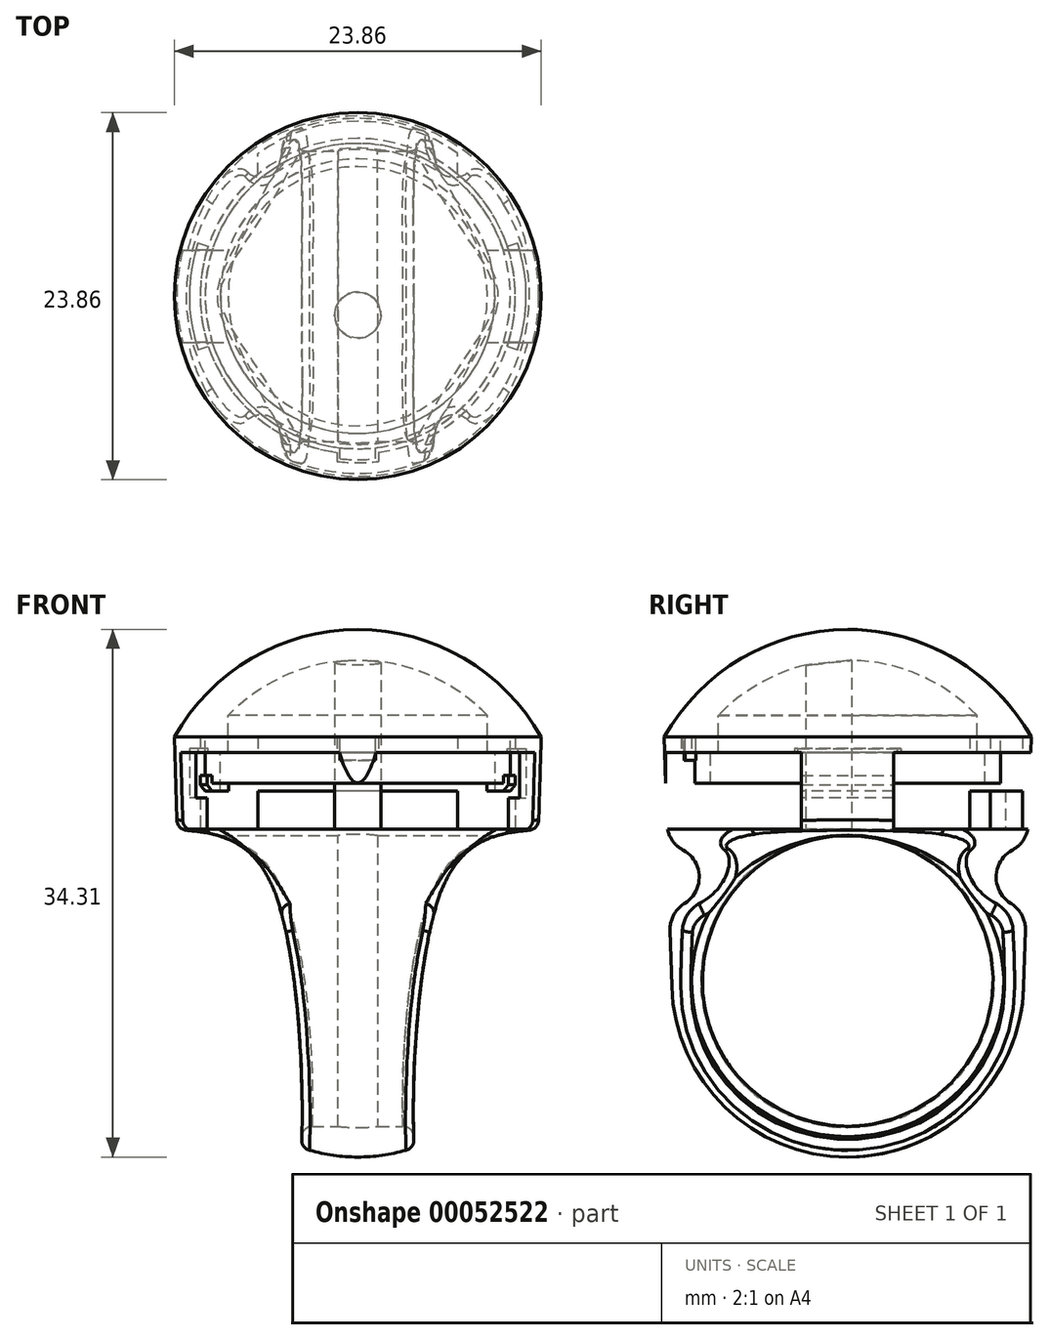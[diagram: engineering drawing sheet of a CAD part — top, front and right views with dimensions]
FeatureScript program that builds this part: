
annotation { "Feature Type Name" : "Feature", "Feature Type Description" : "" }
export const myFeature = defineFeature(function(context is Context, id is Id, definition is map)
    precondition{}
    {
        {
            var Q0;
            Q0=qCreatedBy(makeId("Top.planeOp"),FACE);
            var sketch = newSketch(context, id + "F0", { "sketchPlane" : qUnion([Q0])});
            skArc(sketch, "E0", {"start": v(1.35, -10.16) * mm, "mid": v(9.86, -2.8) * mm, "end": v(6.5, 7.93) * mm});
            skLineSegment(sketch, "E1.rect.left", {"start": v(1.35, -10.75) * mm, "end": v(1.35, -10.16) * mm});
            skLineSegment(sketch, "E1.rect.right", {"start": v(-1.35, -10.75) * mm, "end": v(-1.35, -10.16) * mm});
            skPoint(sketch, "E1.rect.middle", {"position": v(0, -10.25) * mm});
            skPoint(sketch, "E2.orphan", {"position": v(-1.35, -9.75) * mm});
            skPoint(sketch, "E3.orphan", {"position": v(1.35, -9.75) * mm});
            skArc(sketch, "E4", {"start": v(-1.35, -10.75) * mm, "mid": v(0, -10.83) * mm, "end": v(1.35, -10.75) * mm});
            skPoint(sketch, "E4.second.point", {"position": v(1.35, 11.29) * mm});
            skLineSegment(sketch, "E5", {"start": v(-6.5, 9.27) * mm, "end": v(-6.5, 7.93) * mm});
            skLineSegment(sketch, "E6", {"start": v(6.5, 9.27) * mm, "end": v(6.5, 7.93) * mm});
            skArc(sketch, "E7.trimOffspring", {"start": v(-6.5, 7.93) * mm, "mid": v(-9.86, -2.8) * mm, "end": v(-1.35, -10.16) * mm});
            skArc(sketch, "E8.trimOffspring", {"start": v(6.5, 9.27) * mm, "mid": v(0, 11.37) * mm, "end": v(-6.5, 9.27) * mm});
            skSolve(sketch);
        }
        {
            var Q0;
            Q0 = qSketchRegion(id + "F0", true);
            extrude(context, id + "F1", {"entities" : qUnion([Q0]), "depth" : 5 * mm});
        }
        {
            var Q0;
            Q0=qCreatedBy(makeId("Right.planeOp"),FACE);
            var sketch = newSketch(context, id + "F2", { "sketchPlane" : qUnion([Q0])});
            skArc(sketch, "E9", {"start": v(0, -21.3) * mm, "mid": v(7.98, -18.08) * mm, "end": v(11.44, -10.2) * mm});
            skLineSegment(sketch, "E10", {"start": v(11.44, -10.2) * mm, "end": v(11.55, -6.57) * mm});
            skLineSegment(sketch, "E11", {"start": v(0, 13) * mm, "end": v(0, -9.86) * mm});
            skPoint(sketch, "E12.center.orphan", {"position": v(0, -16.43) * mm});
            skArc(sketch, "E13", {"start": v(11.99, 7.98) * mm, "mid": v(6.44, 11.57) * mm, "end": v(0, 13) * mm});
            skLineSegment(sketch, "E14", {"start": v(0, -9.86) * mm, "end": v(0, -21.3) * mm});
            skCircle(sketch, "E15", {"center": v(0, -9.86) * mm, "radius": 9.54 * mm});
            skArc(sketch, "E16", {"start": v(10.7, -1.35) * mm, "mid": v(9.66, -3.05) * mm, "end": v(10.6, -4.8) * mm});
            skLineSegment(sketch, "E17.trimOffspring", {"start": v(11.76, 0.36) * mm, "end": v(11.99, 7.98) * mm});
            skPoint(sketch, "E18.visualSharp", {"position": v(11.72, -1.1) * mm});
            skArc(sketch, "E18.filletArc", {"start": v(10.7, -1.35) * mm, "mid": v(11.46, -0.64) * mm, "end": v(11.76, 0.36) * mm});
            skPoint(sketch, "E19.visualSharp", {"position": v(11.6, -5.1) * mm});
            skArc(sketch, "E19.filletArc", {"start": v(11.55, -6.57) * mm, "mid": v(11.31, -5.56) * mm, "end": v(10.6, -4.8) * mm});
            skSolve(sketch);
        }
        {
            var Q0;
            Q0 = qSketchRegion(id + "F2", true);
            var Q1;
            Q1=sQuery(id+"F2.wireOp",EDGE,"E14");
            revolve(context, id + "F3", {"entities" : qUnion([Q0]), "axis" : qUnion([Q1]), "revolveType" : RevolveType.FULL});
        }
        {
            var Q0;
            Q0=qCreatedBy(makeId("Right.planeOp"),FACE);
            var sketch = newSketch(context, id + "F4", { "sketchPlane" : qUnion([Q0])});
            skCircle(sketch, "E20", {"center": v(0, -9.86) * mm, "radius": 9.45 * mm});
            skSolve(sketch);
        }
        {
            var Q0;
            Q0 = qSketchRegion(id + "F4", true);
            extrude(context, id + "F5", {"entities" : qUnion([Q0]), "operationType" : NewBodyOperationType.REMOVE, "endBound" : BoundingType.SYMMETRIC, "oppositeDirection" : true, "depth" : 25 * mm});
        }
        {
            var Q0;
            Q0=makeQuery(id+"F0.imprint","IMPRINT",FACE,{"disambiguationData":[TD([[makeQuery(id+"F0.imprint","IMPRINT",EDGE,{"derivedFrom":sQuery(id+"F0.wireOp",EDGE,"E0")}),1.0]])]});
            extrude(context, id + "F6", {"entities" : qUnion([Q0]), "operationType" : NewBodyOperationType.REMOVE, "depth" : 25 * mm});
        }
        {
            var Q0;
            Q0=qCreatedBy(makeId("Front.planeOp"),FACE);
            var sketch = newSketch(context, id + "F7", { "sketchPlane" : qUnion([Q0])});
            skLineSegment(sketch, "E21.rect.bottom", {"start": v(-22.02, 6) * mm, "end": v(22.02, 6) * mm});
            skLineSegment(sketch, "E21.rect.top", {"start": v(-22.02, 25.32) * mm, "end": v(22.02, 25.32) * mm});
            skLineSegment(sketch, "E21.rect.left", {"start": v(-22.02, 6) * mm, "end": v(-22.02, 25.32) * mm});
            skLineSegment(sketch, "E21.rect.right", {"start": v(22.02, 6) * mm, "end": v(22.02, 25.32) * mm});
            skPoint(sketch, "E21.rect.middle", {"position": v(0, 15.66) * mm});
            skSolve(sketch);
        }
        {
            var Q0;
            Q0 = qSketchRegion(id + "F7", true);
            extrude(context, id + "F8", {"entities" : qUnion([Q0]), "operationType" : NewBodyOperationType.REMOVE, "endBound" : BoundingType.SYMMETRIC, "oppositeDirection" : true, "depth" : 25 * mm});
        }
        {
            var Q0;
            Q0=qCreatedBy(makeId("Front.planeOp"),FACE);
            var sketch = newSketch(context, id + "F9", { "sketchPlane" : qUnion([Q0])});
            skFitSpline(sketch, "E22", {"points": [v(-11.83, 0) * mm, v(-5.73, -3.33) * mm, v(-3.7, -20.72) * mm, v(-3.75, -20.82) * mm], "startDerivative": vector(19.03, -1.52) * mm, "endDerivative": vector(-1.1, -0.68) * mm});
            skLineSegment(sketch, "E23", {"start": v(-3.73, -20.81) * mm, "end": v(-15.44, -21.38) * mm});
            skLineSegment(sketch, "E24", {"start": v(-15.44, -21.38) * mm, "end": v(-18.85, -6.94) * mm});
            skLineSegment(sketch, "E25", {"start": v(-18.85, -6.94) * mm, "end": v(-11.83, 0) * mm});
            skLineSegment(sketch, "E26", {"start": v(0, -2.22) * mm, "end": v(0, -12.94) * mm});
            skFitSpline(sketch, "E27.MirrorCS", {"points": [v(11.83, 0) * mm, v(5.73, -3.33) * mm, v(3.7, -20.72) * mm, v(3.75, -20.82) * mm], "startDerivative": vector(-19.03, -1.52) * mm, "endDerivative": vector(1.1, -0.68) * mm});
            skLineSegment(sketch, "E28.MirrorCS", {"start": v(18.85, -6.94) * mm, "end": v(11.83, 0) * mm});
            skLineSegment(sketch, "E29.MirrorCS", {"start": v(15.44, -21.38) * mm, "end": v(18.85, -6.94) * mm});
            skLineSegment(sketch, "E30.MirrorCS", {"start": v(3.73, -20.81) * mm, "end": v(15.44, -21.38) * mm});
            skSolve(sketch);
        }
        {
            var Q0;
            Q0 = qSketchRegion(id + "F9", true);
            extrude(context, id + "F10", {"entities" : qUnion([Q0]), "operationType" : NewBodyOperationType.REMOVE, "endBound" : BoundingType.SYMMETRIC, "oppositeDirection" : true, "depth" : 50 * mm});
        }
        {
            var Q0;
            Q0=makeQuery(id+"F10.boolean.opBoolean","INTERSECT",EDGE,{"derivedFrom":[makeQuery(id+"F5.boolean.opBoolean","SPLIT",FACE,{"disambiguationData":[OD(1.0)],"derivedFrom":makeQuery(id+"F3.opRevolve","SWEPT_FACE",FACE,{"disambiguationData":[OSD([sQuery(id+"F2.wireOp",EDGE,"E10")])]})}),makeQuery(id+"F10.opExtrude","SWEPT_FACE",FACE,{"disambiguationData":[OSD([sQuery(id+"F9.wireOp",EDGE,"E22")])]})]});
            var Q1;
            Q1=makeQuery(id+"F10.boolean.opBoolean","INTERSECT",EDGE,{"derivedFrom":[makeQuery(id+"F5.boolean.opBoolean","COPY",FACE,{"disambiguationData":[OD(0.0)],"derivedFrom":makeQuery(id+"F5.opExtrude","SWEPT_FACE",FACE,{"disambiguationData":[OSD([sQuery(id+"F4.wireOp",EDGE,"E20")])]})}),makeQuery(id+"F10.opExtrude","SWEPT_FACE",FACE,{"disambiguationData":[OSD([sQuery(id+"F9.wireOp",EDGE,"E22")])]})]});
            var Q2;
            Q2=makeQuery(id+"F10.boolean.opBoolean","INTERSECT",EDGE,{"derivedFrom":[makeQuery(id+"F5.boolean.opBoolean","COPY",FACE,{"disambiguationData":[OD(1.0)],"derivedFrom":makeQuery(id+"F5.opExtrude","SWEPT_FACE",FACE,{"disambiguationData":[OSD([sQuery(id+"F4.wireOp",EDGE,"E20")])]})}),makeQuery(id+"F10.opExtrude","SWEPT_FACE",FACE,{"disambiguationData":[OSD([sQuery(id+"F9.wireOp",EDGE,"E27.MirrorCS")])]})]});
            var Q3;
            Q3=makeQuery(id+"F10.boolean.opBoolean","INTERSECT",EDGE,{"derivedFrom":[makeQuery(id+"F5.boolean.opBoolean","SPLIT",FACE,{"disambiguationData":[OD(1.0)],"derivedFrom":makeQuery(id+"F3.opRevolve","SWEPT_FACE",FACE,{"disambiguationData":[OSD([sQuery(id+"F2.wireOp",EDGE,"E16")])]})}),makeQuery(id+"F10.opExtrude","SWEPT_FACE",FACE,{"disambiguationData":[OSD([sQuery(id+"F9.wireOp",EDGE,"E27.MirrorCS")])]})]});
            fillet(context, id + "F11", {"entities" : qUnion([Q0, Q1, Q2, Q3]), "radius" : 0.7 * mm, "tangentPropagation" : true, "allowEdgeOverflow" : false});
        }
        {
            var Q0;
            Q0=qCreatedBy(makeId("Right.planeOp"),FACE);
            var sketch = newSketch(context, id + "F12", { "sketchPlane" : qUnion([Q0])});
            skArc(sketch, "E31", {"start": v(11.93, 6) * mm, "mid": v(6.91, 11.12) * mm, "end": v(0, 13) * mm});
            skLineSegment(sketch, "E32", {"start": v(0, 13) * mm, "end": v(18.07, 13) * mm, "construction": true});
            skLineSegment(sketch, "E33", {"start": v(11.93, 6) * mm, "end": v(9.93, 6) * mm});
            skLineSegment(sketch, "E34", {"start": v(9.93, 6) * mm, "end": v(9.93, 5) * mm});
            skLineSegment(sketch, "E35", {"start": v(9.93, 5) * mm, "end": v(8.43, 5) * mm});
            skLineSegment(sketch, "E36", {"start": v(8.43, 5) * mm, "end": v(8.43, 7.4) * mm});
            skArc(sketch, "E37", {"start": v(8.43, 7.4) * mm, "mid": v(4.58, 10.06) * mm, "end": v(0, 11) * mm});
            skLineSegment(sketch, "E38", {"start": v(0, 13) * mm, "end": v(0, 11) * mm});
            skSolve(sketch);
        }
        {
            var Q0;
            Q0=makeQuery(id+"F12.imprint","IMPRINT",FACE,{"disambiguationData":[TD([[makeQuery(id+"F12.imprint","IMPRINT",EDGE,{"derivedFrom":sQuery(id+"F12.wireOp",EDGE,"E31")}),1.0]])]});
            var Q1;
            Q1=sQuery(id+"F12.wireOp",EDGE,"E38");
            revolve(context, id + "F13", {"entities" : qUnion([Q0]), "axis" : qUnion([Q1]), "revolveType" : RevolveType.FULL});
        }
        {
            var Q0;
            Q0=makeQuery(id+"F0.imprint","IMPRINT",FACE,{"disambiguationData":[TD([[makeQuery(id+"F0.imprint","IMPRINT",EDGE,{"derivedFrom":sQuery(id+"F0.wireOp",EDGE,"E0")}),1.0]])]});
            var sketch = newSketch(context, id + "F14", { "sketchPlane" : qUnion([Q0])});
            skCircle(sketch, "E39", {"center": v(0, -1.23) * mm, "radius": 1.5 * mm});
            skSolve(sketch);
        }
        {
            var Q0;
            Q0 = qSketchRegion(id + "F14", true);
            var Q1;
            Q1=makeQuery(id+"F13.opRevolve","SWEPT_FACE",FACE,{"disambiguationData":[OSD([sQuery(id+"F12.wireOp",EDGE,"E37")])]});
            extrude(context, id + "F15", {"entities" : qUnion([Q0]), "operationType" : NewBodyOperationType.ADD, "endBound" : BoundingType.UP_TO_SURFACE, "endBoundEntityFace" : qUnion([Q1]), "depth" : 25 * mm});
        }
        {
            var Q0;
            Q0=qCreatedBy(makeId("Front.planeOp"),FACE);
            var sketch = newSketch(context, id + "F16", { "sketchPlane" : qUnion([Q0])});
            skLineSegment(sketch, "E40.bottom", {"start": v(18.44, 0) * mm, "end": v(-11.63, 0) * mm});
            skLineSegment(sketch, "E40.top", {"start": v(18.44, 3.03) * mm, "end": v(-11.63, 3.03) * mm});
            skLineSegment(sketch, "E40.left", {"start": v(18.44, 0) * mm, "end": v(18.44, 3.03) * mm});
            skLineSegment(sketch, "E40.right", {"start": v(-11.63, 0) * mm, "end": v(-11.63, 3.03) * mm});
            skSolve(sketch);
        }
        {
            var Q0;
            Q0=makeQuery(id+"F13.opRevolve","SWEPT_FACE",FACE,{"disambiguationData":[OSD([sQuery(id+"F12.wireOp",EDGE,"E35")])]});
            var sketch = newSketch(context, id + "F17", { "sketchPlane" : qUnion([Q0])});
            skArc(sketch, "E41", {"start": v(-9.46, 3) * mm, "mid": v(-9.93, 0) * mm, "end": v(-9.46, -3) * mm});
            skArc(sketch, "E42", {"start": v(-8.4, 3) * mm, "mid": v(-8.93, 0) * mm, "end": v(-8.4, -3) * mm});
            skLineSegment(sketch, "E43", {"start": v(-9.46, 3) * mm, "end": v(-8.4, 3) * mm});
            skLineSegment(sketch, "E44", {"start": v(-9.46, -3) * mm, "end": v(-8.4, -3) * mm});
            skLineSegment(sketch, "E45.trimOffspring", {"start": v(8.4, 3) * mm, "end": v(9.46, 3) * mm});
            skArc(sketch, "E46.trimOffspring", {"start": v(8.4, -3) * mm, "mid": v(8.93, 0) * mm, "end": v(8.4, 3) * mm});
            skArc(sketch, "E47.trimOffspring", {"start": v(9.46, -3) * mm, "mid": v(9.93, 0) * mm, "end": v(9.46, 3) * mm});
            skLineSegment(sketch, "E48.trimOffspring", {"start": v(8.4, -3) * mm, "end": v(9.46, -3) * mm});
            skSolve(sketch);
        }
        {
            var Q0;
            Q0 = qSketchRegion(id + "F17", true);
            extrude(context, id + "F18", {"entities" : qUnion([Q0]), "operationType" : NewBodyOperationType.ADD, "depth" : 2.5 * mm});
        }
        {
            var Q0;
            Q0=makeQuery(id+"F18.opExtrude","SWEPT_FACE",FACE,{"disambiguationData":[OSD([sQuery(id+"F17.wireOp",EDGE,"E43")])]});
            var sketch = newSketch(context, id + "F19", { "sketchPlane" : qUnion([Q0])});
            skLineSegment(sketch, "E49", {"start": v(-9.46, 3.5) * mm, "end": v(-9.46, 2.5) * mm});
            skLineSegment(sketch, "E50", {"start": v(-9.46, 3.5) * mm, "end": v(-10.16, 3.5) * mm});
            skLineSegment(sketch, "E51", {"start": v(-10.16, 3.5) * mm, "end": v(-10.16, 3.33) * mm});
            skLineSegment(sketch, "E52", {"start": v(-10.16, 3.33) * mm, "end": v(-9.46, 2.5) * mm});
            skSolve(sketch);
        }
        {
            var Q0;
            Q0 = qSketchRegion(id + "F19", true);
            var Q1;
            Q1=makeQuery(id+"F18.boolean.opBoolean","MERGE",FACE,{"derivedFrom":[makeQuery(id+"F13.opRevolve","SWEPT_FACE",FACE,{"disambiguationData":[OSD([sQuery(id+"F12.wireOp",EDGE,"E34")])]}),makeQuery(id+"F18.opExtrude","SWEPT_FACE",FACE,{"disambiguationData":[OSD([sQuery(id+"F17.wireOp",EDGE,"E41")])]}),makeQuery(id+"F18.opExtrude","SWEPT_FACE",FACE,{"disambiguationData":[OSD([sQuery(id+"F17.wireOp",EDGE,"E47.trimOffspring")])]})]});
            revolve(context, id + "F20", {"operationType" : NewBodyOperationType.ADD, "entities" : qUnion([Q0]), "axis" : qUnion([Q1]), "revolveType" : RevolveType.FULL});
        }
        {
            var Q0;
            Q0=makeQuery(id+"F0.imprint","IMPRINT",FACE,{"disambiguationData":[TD([[makeQuery(id+"F0.imprint","IMPRINT",EDGE,{"derivedFrom":sQuery(id+"F0.wireOp",EDGE,"E0")}),1.0]])]});
            var sketch = newSketch(context, id + "F21", { "sketchPlane" : qUnion([Q0])});
            skLineSegment(sketch, "E53.bottom", {"start": v(-16.33, -11.84) * mm, "end": v(16.46, -11.84) * mm});
            skLineSegment(sketch, "E53.top", {"start": v(-16.33, -3) * mm, "end": v(16.46, -3) * mm});
            skLineSegment(sketch, "E53.left", {"start": v(-16.33, -11.84) * mm, "end": v(-16.33, -3) * mm});
            skLineSegment(sketch, "E53.right", {"start": v(16.46, -11.84) * mm, "end": v(16.46, -3) * mm});
            skLineSegment(sketch, "E54.bottom", {"start": v(-16.02, 3) * mm, "end": v(13.6, 3) * mm});
            skLineSegment(sketch, "E54.top", {"start": v(-16.02, 11.98) * mm, "end": v(13.6, 11.98) * mm});
            skLineSegment(sketch, "E54.left", {"start": v(-16.02, 3) * mm, "end": v(-16.02, 11.98) * mm});
            skLineSegment(sketch, "E54.right", {"start": v(13.6, 3) * mm, "end": v(13.6, 11.98) * mm});
            skSolve(sketch);
        }
        {
            var Q0;
            Q0 = qSketchRegion(id + "F21", true);
            extrude(context, id + "F22", {"entities" : qUnion([Q0]), "operationType" : NewBodyOperationType.REMOVE, "depth" : 5 * mm});
        }
        {
            var Q0;
            Q0=qCreatedBy(makeId("Front.planeOp"),FACE);
            var sketch = newSketch(context, id + "F23", { "sketchPlane" : qUnion([Q0])});
            skLineSegment(sketch, "E55", {"start": v(-10.25, 5.24) * mm, "end": v(-10.95, 5.24) * mm});
            skLineSegment(sketch, "E56", {"start": v(-10.95, 5.24) * mm, "end": v(-10.95, 2.05) * mm});
            skLineSegment(sketch, "E57", {"start": v(-10.95, 2.05) * mm, "end": v(-10.25, 2.05) * mm});
            skLineSegment(sketch, "E58", {"start": v(-10.25, 2.05) * mm, "end": v(-10.25, 5.24) * mm});
            skLineSegment(sketch, "E59", {"start": v(0, 6.4) * mm, "end": v(0, 4.6) * mm});
            skLineSegment(sketch, "E60.MirrorCS", {"start": v(10.95, 2.05) * mm, "end": v(10.25, 2.05) * mm});
            skLineSegment(sketch, "E61.MirrorCS", {"start": v(10.25, 5.24) * mm, "end": v(10.95, 5.24) * mm});
            skLineSegment(sketch, "E62.MirrorCS", {"start": v(10.95, 5.24) * mm, "end": v(10.95, 2.05) * mm});
            skLineSegment(sketch, "E63.MirrorCS", {"start": v(10.25, 2.05) * mm, "end": v(10.25, 5.24) * mm});
            skSolve(sketch);
        }
        {
            var Q0;
            Q0 = qSketchRegion(id + "F23", true);
            var Q1;
            Q1=makeQuery(id+"F8.boolean.opBoolean","INTERSECT",EDGE,{"derivedFrom":[makeQuery(id+"F3.opRevolve","SWEPT_FACE",FACE,{"disambiguationData":[OSD([sQuery(id+"F2.wireOp",EDGE,"E17.trimOffspring")])]}),makeQuery(id+"F8.opExtrude","SWEPT_FACE",FACE,{"disambiguationData":[OSD([sQuery(id+"F7.wireOp",EDGE,"E21.rect.bottom")])]})]});
            revolve(context, id + "F24", {"operationType" : NewBodyOperationType.REMOVE, "entities" : qUnion([Q0]), "axis" : qUnion([Q1]), "revolveType" : RevolveType.SYMMETRIC, "angle" : 37 * degree});
        }
        {
            var Q0;
            Q0=makeQuery(id+"F13.opRevolve","SWEPT_FACE",FACE,{"disambiguationData":[OSD([sQuery(id+"F12.wireOp",EDGE,"E33")])]});
            var sketch = newSketch(context, id + "F25", { "sketchPlane" : qUnion([Q0])});
            skLineSegment(sketch, "E64", {"start": v(-1.15, 10.57) * mm, "end": v(-1.15, 9.86) * mm});
            skLineSegment(sketch, "E65", {"start": v(1.15, 10.57) * mm, "end": v(1.15, 9.86) * mm});
            skArc(sketch, "E66", {"start": v(1.15, 9.86) * mm, "mid": v(0, 9.93) * mm, "end": v(-1.15, 9.86) * mm});
            skArc(sketch, "E67", {"start": v(1.15, 10.57) * mm, "mid": v(0, 10.63) * mm, "end": v(-1.15, 10.57) * mm});
            skSolve(sketch);
        }
        {
            var Q0;
            Q0 = qSketchRegion(id + "F25", true);
            extrude(context, id + "F26", {"entities" : qUnion([Q0]), "operationType" : NewBodyOperationType.ADD, "depth" : 1.5 * mm});
        }
        {
            var Q0;
            Q0=makeQuery(id+"F0.imprint","IMPRINT",FACE,{"disambiguationData":[TD([[makeQuery(id+"F0.imprint","IMPRINT",EDGE,{"derivedFrom":sQuery(id+"F0.wireOp",EDGE,"E0")}),1.0]])]});
            var sketch = newSketch(context, id + "F27", { "sketchPlane" : qUnion([Q0])});
            skArc(sketch, "E68", {"start": v(6.5, 7.93) * mm, "mid": v(0, 10.25) * mm, "end": v(-6.5, 7.93) * mm});
            skLineSegment(sketch, "E69", {"start": v(6.5, 9.27) * mm, "end": v(6.5, 7.93) * mm});
            skLineSegment(sketch, "E70", {"start": v(-6.5, 9.27) * mm, "end": v(-6.5, 7.93) * mm});
            skArc(sketch, "E71", {"start": v(6.5, 9.27) * mm, "mid": v(0, 11.37) * mm, "end": v(-6.5, 9.27) * mm});
            skSolve(sketch);
        }
        {
            var Q0;
            Q0 = qSketchRegion(id + "F27", true);
            extrude(context, id + "F28", {"entities" : qUnion([Q0]), "operationType" : NewBodyOperationType.ADD, "depth" : 2.5 * mm});
        }
        {
            var Q0;
            Q0=makeQuery(id+"F13.opRevolve","SWEPT_FACE",FACE,{"disambiguationData":[OSD([sQuery(id+"F12.wireOp",EDGE,"E35")])]});
            var sketch = newSketch(context, id + "F29", { "sketchPlane" : qUnion([Q0])});
            skCircle(sketch, "E72", {"center": v(0, 0) * mm, "radius": 9.93 * mm});
            skCircle(sketch, "E73", {"center": v(0, 0) * mm, "radius": 8.93 * mm});
            skSolve(sketch);
        }
        {
            var Q0;
            Q0 = qSketchRegion(id + "F29", true);
            extrude(context, id + "F30", {"entities" : qUnion([Q0]), "operationType" : NewBodyOperationType.ADD, "depth" : 2 * mm});
        }
    });
